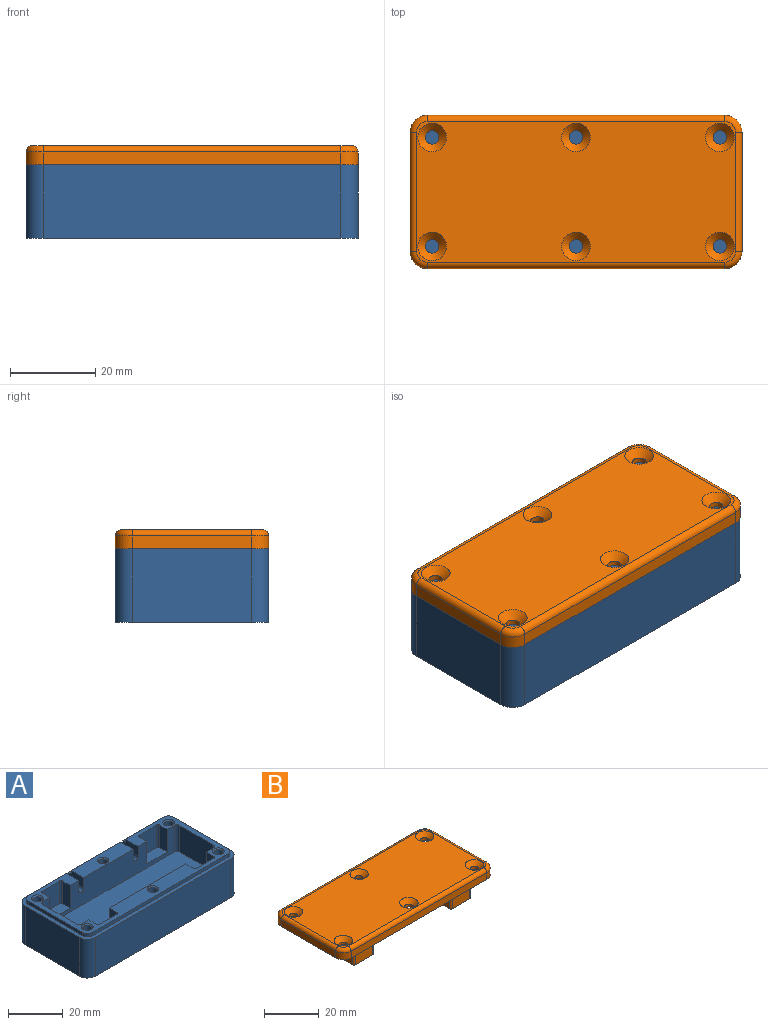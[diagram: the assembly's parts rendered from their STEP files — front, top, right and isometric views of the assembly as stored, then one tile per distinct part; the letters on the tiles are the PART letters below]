
ASSEMBLY  parts=2 mates=1
PART A: 80 faces, bbox 78x36x18.8 mm
  f0: plane 25.5x6.45mm, normal (0,0,1), area 150.3mm2, adj f1,f3,f67,f72,f77
  f1: plane 68x11.8mm, normal (0,-1,0), area 563mm2, adj f0,f6,f7,f8,f11,f12,f28,f29
  f2: plane 19.75x1.5mm, normal (0,1,0), area 29.6mm2, adj f4,f6,f41,f70
  f3: plane 25.5x1.5mm, normal (0,1,0), area 38.2mm2, adj f0,f5,f67,f72
  f4: plane 78x36mm, normal (0,0,1), area 278.9mm2, adj f2,f39,f40,f41,f42,f43,f44,f45
  f5: plane 25.5x1.5mm, normal (0,0,1), area 38.2mm2, adj f3,f52,f67,f72
  f6: plane 75x33mm, normal (0,0,1), area 584.1mm2, adj f1,f2,f10,f11,f12,f13,f14,f15
  f7: plane 10.6x4.75mm, normal (0,0,1), area 50.1mm2, adj f1,f10,f11,f34,f35,f36
  f8: plane 10.6x4.75mm, normal (0,0,1), area 50.1mm2, adj f1,f29,f30,f31,f32,f33
  f9: plane 10.6x4.75mm, normal (0,0,1), area 50.1mm2, adj f15,f16,f17,f18,f19,f20
  f10: cylinder r=0.8mm len=10mm, axis (0,0,1), area 12.6mm2, adj f6,f7,f11,f36
  f11: plane 10x3.95mm, normal (1,0,0), area 39.5mm2, adj f1,f6,f7,f10
  f12: cylinder r=1.3mm len=11.8mm, axis (0,0,1), area 24.1mm2, adj f1,f6,f13,f38
  f13: plane 17.5x11.8mm, normal (1,0,0), area 206.5mm2, adj f6,f12,f14,f38
  f14: cylinder r=1.3mm len=11.8mm, axis (0,0,1), area 24.1mm2, adj f6,f13,f15,f38
  f15: plane 68x11.8mm, normal (0,1,0), area 590.4mm2, adj f6,f9,f14,f16,f20,f21,f25,f26
  f16: plane 10x3.95mm, normal (1,0,0), area 39.5mm2, adj f6,f9,f15,f17
  f17: cylinder r=0.8mm len=10mm, axis (0,0,1), area 12.6mm2, adj f6,f9,f16,f18
  f18: plane 10x9mm, normal (0,1,0), area 90mm2, adj f6,f9,f17,f19
  f19: cylinder r=0.8mm len=10mm, axis (0,0,1), area 12.6mm2, adj f6,f9,f18,f20
  f20: plane 10x3.95mm, normal (-1,0,0), area 39.5mm2, adj f6,f9,f15,f19
  f21: plane 10x3.95mm, normal (1,0,0), area 39.5mm2, adj f6,f15,f22,f37
  f22: cylinder r=0.8mm len=10mm, axis (0,0,1), area 12.6mm2, adj f6,f21,f23,f37
  f23: plane 10x9mm, normal (0,1,0), area 90mm2, adj f6,f22,f24,f37
  f24: cylinder r=0.8mm len=10mm, axis (0,0,1), area 12.6mm2, adj f6,f23,f25,f37
  f25: plane 10x3.95mm, normal (-1,0,0), area 39.5mm2, adj f6,f15,f24,f37
  f26: cylinder r=1.3mm len=11.8mm, axis (0,0,1), area 24.1mm2, adj f6,f15,f27,f38
  f27: plane 17.5x11.8mm, normal (-1,0,0), area 206.5mm2, adj f6,f26,f28,f38
  f28: cylinder r=1.3mm len=11.8mm, axis (0,0,1), area 24.1mm2, adj f1,f6,f27,f38
  f29: plane 10x3.95mm, normal (-1,0,0), area 39.5mm2, adj f1,f6,f8,f30
  f30: cylinder r=0.8mm len=10mm, axis (0,0,1), area 12.6mm2, adj f6,f8,f29,f31
  f31: plane 10x9mm, normal (0,-1,0), area 90mm2, adj f6,f8,f30,f32
  f32: cylinder r=0.8mm len=10mm, axis (0,0,1), area 12.6mm2, adj f6,f8,f31,f33
  f33: plane 10x3.95mm, normal (1,0,0), area 39.5mm2, adj f1,f6,f8,f32
  f34: plane 10x3.95mm, normal (-1,0,0), area 39.5mm2, adj f1,f6,f7,f35
  f35: cylinder r=0.8mm len=10mm, axis (0,0,1), area 12.6mm2, adj f6,f7,f34,f36
  f36: plane 10x9mm, normal (0,-1,0), area 90mm2, adj f6,f7,f10,f35
  f37: plane 10.6x4.75mm, normal (0,0,1), area 50.1mm2, adj f15,f21,f22,f23,f24,f25
  f38: plane 70.6x20.1mm, normal (0,0,1), area 1417.6mm2, adj f1,f12,f13,f14,f15,f26,f27,f28
  f39: cylinder r=2.5mm len=2.5mm, axis (0,0,1), area 5.9mm2, adj f4,f6,f40,f46
  f40: plane 19.75x1.5mm, normal (0,1,0), area 29.6mm2, adj f4,f6,f39,f69
  f41: cylinder r=2.5mm len=2.5mm, axis (0,0,1), area 5.9mm2, adj f2,f4,f6,f42
  f42: plane 28x1.5mm, normal (1,0,0), area 42mm2, adj f4,f6,f41,f43
  f43: cylinder r=2.5mm len=2.5mm, axis (0,0,1), area 5.9mm2, adj f4,f6,f42,f44
  f44: plane 70x1.5mm, normal (0,-1,0), area 105mm2, adj f4,f6,f43,f45
  f45: cylinder r=2.5mm len=2.5mm, axis (0,0,1), area 5.9mm2, adj f4,f6,f44,f46
  f46: plane 28x1.5mm, normal (-1,0,0), area 42mm2, adj f4,f6,f39,f45
  f47: cylinder r=4mm len=17.3mm, axis (0,0,-1), area 108.7mm2, adj f4,f48,f54,f79
  f48: plane 70x17.3mm, normal (0,-1,0), area 1211mm2, adj f4,f47,f49,f79
  f49: cylinder r=4mm len=17.3mm, axis (0,0,-1), area 108.7mm2, adj f4,f48,f50,f79
  f50: plane 28x17.3mm, normal (-1,0,0), area 484.4mm2, adj f4,f49,f51,f79
  f51: cylinder r=4mm len=17.3mm, axis (0,0,-1), area 108.7mm2, adj f4,f50,f52,f79
  f52: plane 70x17.3mm, normal (0,1,0), area 1191.1mm2, adj f4,f5,f51,f53,f67,f68,f69,f70
  f53: cylinder r=4mm len=17.3mm, axis (0,0,-1), area 108.7mm2, adj f4,f52,f54,f79
  f54: plane 28x17.3mm, normal (1,0,0), area 484.4mm2, adj f4,f47,f53,f79
  f55: cylinder r=1.62mm len=5.5mm, axis (0,0,1), area 56.2mm2, adj f56,f76
  f56: plane 3.25x3.25mm, normal (0,0,1), area 8.3mm2, adj f55
  f57: cylinder r=1.62mm len=5.5mm, axis (0,0,1), area 56.2mm2, adj f58,f77
  f58: plane 3.25x3.25mm, normal (0,0,1), area 8.3mm2, adj f57
  f59: cylinder r=1.62mm len=5.5mm, axis (0,0,1), area 56.2mm2, adj f60,f78
  f60: plane 3.25x3.25mm, normal (0,0,1), area 8.3mm2, adj f59
  f61: cylinder r=1.62mm len=5.5mm, axis (0,0,1), area 56.2mm2, adj f62,f73
  f62: plane 3.25x3.25mm, normal (0,0,1), area 8.3mm2, adj f61
  f63: cylinder r=1.62mm len=5.5mm, axis (0,0,1), area 56.2mm2, adj f64,f74
  f64: plane 3.25x3.25mm, normal (0,0,1), area 8.3mm2, adj f63
  f65: cylinder r=1.62mm len=5.5mm, axis (0,0,1), area 56.2mm2, adj f66,f75
  f66: plane 3.25x3.25mm, normal (0,0,1), area 8.3mm2, adj f65
  f67: plane 7.95x4.5mm, normal (-1,0,0), area 33.5mm2, adj f0,f1,f3,f5,f52,f68
  f68: cylinder r=1.25mm len=7.95mm, axis (0,1,0), area 31.2mm2, adj f1,f52,f67,f69
  f69: plane 7.95x4.5mm, normal (1,0,0), area 33.5mm2, adj f1,f4,f6,f40,f52,f68
  f70: plane 7.95x4.5mm, normal (-1,0,0), area 33.5mm2, adj f1,f2,f4,f6,f52,f71
  f71: cylinder r=1.25mm len=7.95mm, axis (0,1,0), area 31.2mm2, adj f1,f52,f70,f72
  f72: plane 7.95x4.5mm, normal (1,0,0), area 33.5mm2, adj f0,f1,f3,f5,f52,f71
  f73: cone r=1.62mm half-angle=45deg, axis (0,0,1), area 8.3mm2, adj f6,f61
  f74: cone r=1.62mm half-angle=45deg, axis (0,0,1), area 8.3mm2, adj f6,f63
  f75: cone r=1.62mm half-angle=45deg, axis (0,0,1), area 8.3mm2, adj f6,f65
  f76: cone r=1.62mm half-angle=45deg, axis (0,0,1), area 8.3mm2, adj f6,f55
  f77: cone r=1.62mm half-angle=45deg, axis (0,0,1), area 8.3mm2, adj f0,f57
  f78: cone r=1.62mm half-angle=45deg, axis (0,0,1), area 8.3mm2, adj f6,f59
  f79: plane 78x36mm, normal (0,0,-1), area 2794.3mm2, adj f47,f48,f49,f50,f51,f52,f53,f54
PART B: 84 faces, bbox 78.7x36.7x12 mm
  f0: plane 70.4x19.9mm, normal (0,0,-1), area 1358.1mm2, adj f11,f15,f16,f17,f21,f22,f23,f24
  f1: cylinder r=4mm len=4mm, axis (0,0,1), area 18.8mm2, adj f2,f8,f61,f83
  f2: plane 70x3mm, normal (0,1,0), area 210mm2, adj f1,f3,f59,f83
  f3: cylinder r=4mm len=4mm, axis (0,0,1), area 18.8mm2, adj f2,f4,f57,f83
  f4: plane 28x3mm, normal (-1,0,0), area 84mm2, adj f3,f5,f55,f83
  f5: cylinder r=4mm len=4mm, axis (0,0,1), area 18.8mm2, adj f4,f6,f56,f83
  f6: plane 70x3mm, normal (0,-1,0), area 210mm2, adj f5,f7,f58,f83
  f7: cylinder r=4mm len=4mm, axis (0,0,1), area 18.8mm2, adj f6,f8,f60,f83
  f8: plane 28x3mm, normal (1,0,0), area 84mm2, adj f1,f7,f62,f83
  f9: plane 75.1x33.1mm, normal (0,0,-1), area 835.5mm2, adj f11,f12,f13,f14,f15,f16,f17,f18
  f10: plane 75x33mm, normal (0,0,1), area 2256.8mm2, adj f55,f56,f57,f58,f59,f60,f61,f62
  f11: plane 9x5.05mm, normal (-1,0,0), area 36.9mm2, adj f0,f9,f12,f42,f47,f48,f53
  f12: cylinder r=0.7mm len=9mm, axis (0,0,1), area 9.9mm2, adj f9,f11,f13,f48
  f13: plane 9x9mm, normal (0,1,0), area 81mm2, adj f9,f12,f14,f48
  f14: cylinder r=0.7mm len=9mm, axis (0,0,1), area 9.9mm2, adj f9,f13,f15,f48
  f15: plane 9x5.05mm, normal (1,0,0), area 36.9mm2, adj f0,f9,f14,f16,f47,f48,f53
  f16: plane 39.6x0.8mm, normal (0,1,0), area 31.7mm2, adj f0,f9,f15,f17
  f17: plane 9x5.05mm, normal (-1,0,0), area 36.9mm2, adj f0,f9,f16,f18,f45,f46,f54
  f18: cylinder r=0.7mm len=9mm, axis (0,0,1), area 9.9mm2, adj f9,f17,f19,f46
  f19: plane 9x9mm, normal (0,1,0), area 81mm2, adj f9,f18,f20,f46
  f20: cylinder r=0.7mm len=9mm, axis (0,0,1), area 9.9mm2, adj f9,f19,f21,f46
  f21: plane 9x5.05mm, normal (1,0,0), area 36.9mm2, adj f0,f9,f20,f22,f45,f46,f54
  f22: plane 3.8x0.8mm, normal (0,1,0), area 3mm2, adj f0,f9,f21,f23
  f23: cylinder r=1.2mm len=1.2mm, axis (0,0,1), area 1.5mm2, adj f0,f9,f22,f24
  f24: plane 17.5x0.8mm, normal (1,0,0), area 14mm2, adj f0,f9,f23,f25
  f25: cylinder r=1.2mm len=1.2mm, axis (0,0,1), area 1.5mm2, adj f0,f9,f24,f26
  f26: plane 3.8x0.8mm, normal (0,-1,0), area 3mm2, adj f0,f9,f25,f27
  f27: plane 9x5.05mm, normal (1,0,0), area 36.9mm2, adj f0,f9,f26,f28,f43,f44,f52
  f28: cylinder r=0.7mm len=9mm, axis (0,0,1), area 9.9mm2, adj f9,f27,f29,f44
  f29: plane 9x9mm, normal (0,-1,0), area 81mm2, adj f9,f28,f30,f44
  f30: cylinder r=0.7mm len=9mm, axis (0,0,1), area 9.9mm2, adj f9,f29,f31,f44
  f31: plane 9x5.05mm, normal (-1,0,0), area 36.9mm2, adj f0,f9,f30,f32,f43,f44,f52
  f32: plane 39.6x0.8mm, normal (0,-1,0), area 31.7mm2, adj f0,f9,f31,f33
  f33: plane 9x5.05mm, normal (1,0,0), area 36.9mm2, adj f0,f9,f32,f34,f49,f50,f51
  f34: cylinder r=0.7mm len=9mm, axis (0,0,1), area 9.9mm2, adj f9,f33,f35,f50
  f35: plane 9x9mm, normal (0,-1,0), area 81mm2, adj f9,f34,f36,f50
  f36: cylinder r=0.7mm len=9mm, axis (0,0,1), area 9.9mm2, adj f9,f35,f37,f50
  f37: plane 9x5.05mm, normal (-1,0,0), area 36.9mm2, adj f0,f9,f36,f38,f49,f50,f51
  f38: plane 3.8x0.8mm, normal (0,-1,0), area 3mm2, adj f0,f9,f37,f39
  f39: cylinder r=1.2mm len=1.2mm, axis (0,0,1), area 1.5mm2, adj f0,f9,f38,f40
  f40: plane 17.5x0.8mm, normal (-1,0,0), area 14mm2, adj f0,f9,f39,f41
  f41: cylinder r=1.2mm len=1.2mm, axis (0,0,1), area 1.5mm2, adj f0,f9,f40,f42
  f42: plane 3.8x0.8mm, normal (0,1,0), area 3mm2, adj f0,f9,f11,f41
  f43: plane 10.4x7.2mm, normal (0,1,0), area 74.9mm2, adj f27,f31,f44,f52
  f44: plane 10.4x4.75mm, normal (0,0,-1), area 49.2mm2, adj f27,f28,f29,f30,f31,f43
  f45: plane 10.4x7.2mm, normal (0,-1,0), area 74.9mm2, adj f17,f21,f46,f54
  f46: plane 10.4x4.75mm, normal (0,0,-1), area 49.2mm2, adj f17,f18,f19,f20,f21,f45
  f47: plane 10.4x7.2mm, normal (0,-1,0), area 74.9mm2, adj f11,f15,f48,f53
  f48: plane 10.4x4.75mm, normal (0,0,-1), area 49.2mm2, adj f11,f12,f13,f14,f15,f47
  f49: plane 10.4x7.2mm, normal (0,1,0), area 74.9mm2, adj f33,f37,f50,f51
  f50: plane 10.4x4.75mm, normal (0,0,-1), area 49.2mm2, adj f33,f34,f35,f36,f37,f49
  f51: plane 10.4x1mm, normal (0,0.71,-0.71), area 14.7mm2, adj f0,f33,f37,f49
  f52: plane 10.4x1mm, normal (0,0.71,-0.71), area 14.7mm2, adj f0,f27,f31,f43
  f53: plane 10.4x1mm, normal (0,-0.71,-0.71), area 14.7mm2, adj f0,f11,f15,f47
  f54: plane 10.4x1mm, normal (0,-0.71,-0.71), area 14.7mm2, adj f0,f17,f21,f45
  f55: cylinder r=1.5mm len=28mm, axis (0,-1,0), area 66mm2, adj f4,f10,f56,f57
  f56: torus R=2.5mm, axis (0,0,1), area 12.8mm2, adj f5,f10,f55,f58
  f57: torus R=2.5mm, axis (0,0,1), area 12.8mm2, adj f3,f10,f55,f59
  f58: cylinder r=1.5mm len=70mm, axis (1,0,0), area 164.9mm2, adj f6,f10,f56,f60
  f59: cylinder r=1.5mm len=70mm, axis (-1,0,0), area 164.9mm2, adj f2,f10,f57,f61
  f60: torus R=2.5mm, axis (0,0,1), area 12.8mm2, adj f7,f10,f58,f62
  f61: torus R=2.5mm, axis (0,0,1), area 12.8mm2, adj f1,f10,f59,f62
  f62: cylinder r=1.5mm len=28mm, axis (0,1,0), area 66mm2, adj f8,f10,f60,f61
  f63: cylinder r=1.6mm len=3.2mm, axis (0,0,1), area 12.5mm2, adj f9,f64
  f64: cone r=1.6mm half-angle=45deg, axis (0,0,1), area 38.8mm2, adj f10,f63
  f65: cylinder r=1.6mm len=3.2mm, axis (0,0,1), area 12.5mm2, adj f9,f66
  f66: cone r=1.6mm half-angle=45deg, axis (0,0,1), area 38.8mm2, adj f10,f65
  f67: cylinder r=1.6mm len=3.2mm, axis (0,0,1), area 12.5mm2, adj f9,f68
  f68: cone r=1.6mm half-angle=45deg, axis (0,0,1), area 38.8mm2, adj f10,f67
  f69: cylinder r=1.6mm len=3.2mm, axis (0,0,1), area 12.5mm2, adj f9,f70
  f70: cone r=1.6mm half-angle=45deg, axis (0,0,1), area 38.8mm2, adj f10,f69
  f71: cylinder r=1.6mm len=3.2mm, axis (0,0,1), area 12.5mm2, adj f9,f72
  f72: cone r=1.6mm half-angle=45deg, axis (0,0,1), area 38.8mm2, adj f10,f71
  f73: cylinder r=1.6mm len=3.2mm, axis (0,0,1), area 12.5mm2, adj f9,f74
  f74: cone r=1.6mm half-angle=45deg, axis (0,0,1), area 38.8mm2, adj f10,f73
  f75: cylinder r=2.55mm len=2.55mm, axis (0,0,1), area 6mm2, adj f9,f76,f82,f83
  f76: plane 70x1.5mm, normal (0,-1,0), area 105mm2, adj f9,f75,f77,f83
  f77: cylinder r=2.55mm len=2.55mm, axis (0,0,1), area 6mm2, adj f9,f76,f78,f83
  f78: plane 28x1.5mm, normal (1,0,0), area 42mm2, adj f9,f77,f79,f83
  f79: cylinder r=2.55mm len=2.55mm, axis (0,0,1), area 6mm2, adj f9,f78,f80,f83
  f80: plane 70x1.5mm, normal (0,1,0), area 105mm2, adj f9,f79,f81,f83
  f81: cylinder r=2.55mm len=2.55mm, axis (0,0,1), area 6mm2, adj f9,f80,f82,f83
  f82: plane 28x1.5mm, normal (-1,0,0), area 42mm2, adj f9,f75,f81,f83
  f83: plane 78x36mm, normal (0,0,-1), area 314mm2, adj f1,f2,f3,f4,f5,f6,f7,f8
PLACE A t=(0.78,1.09,5.13)mm fixed
PLACE B rot(axis=(0,0,1),0deg) t=(0.78,1.09,-18.07)mm
MATE fastened A.f4 <-> B.f83  axis (0,0,1) through (39.78,1.09,17.43)mm
